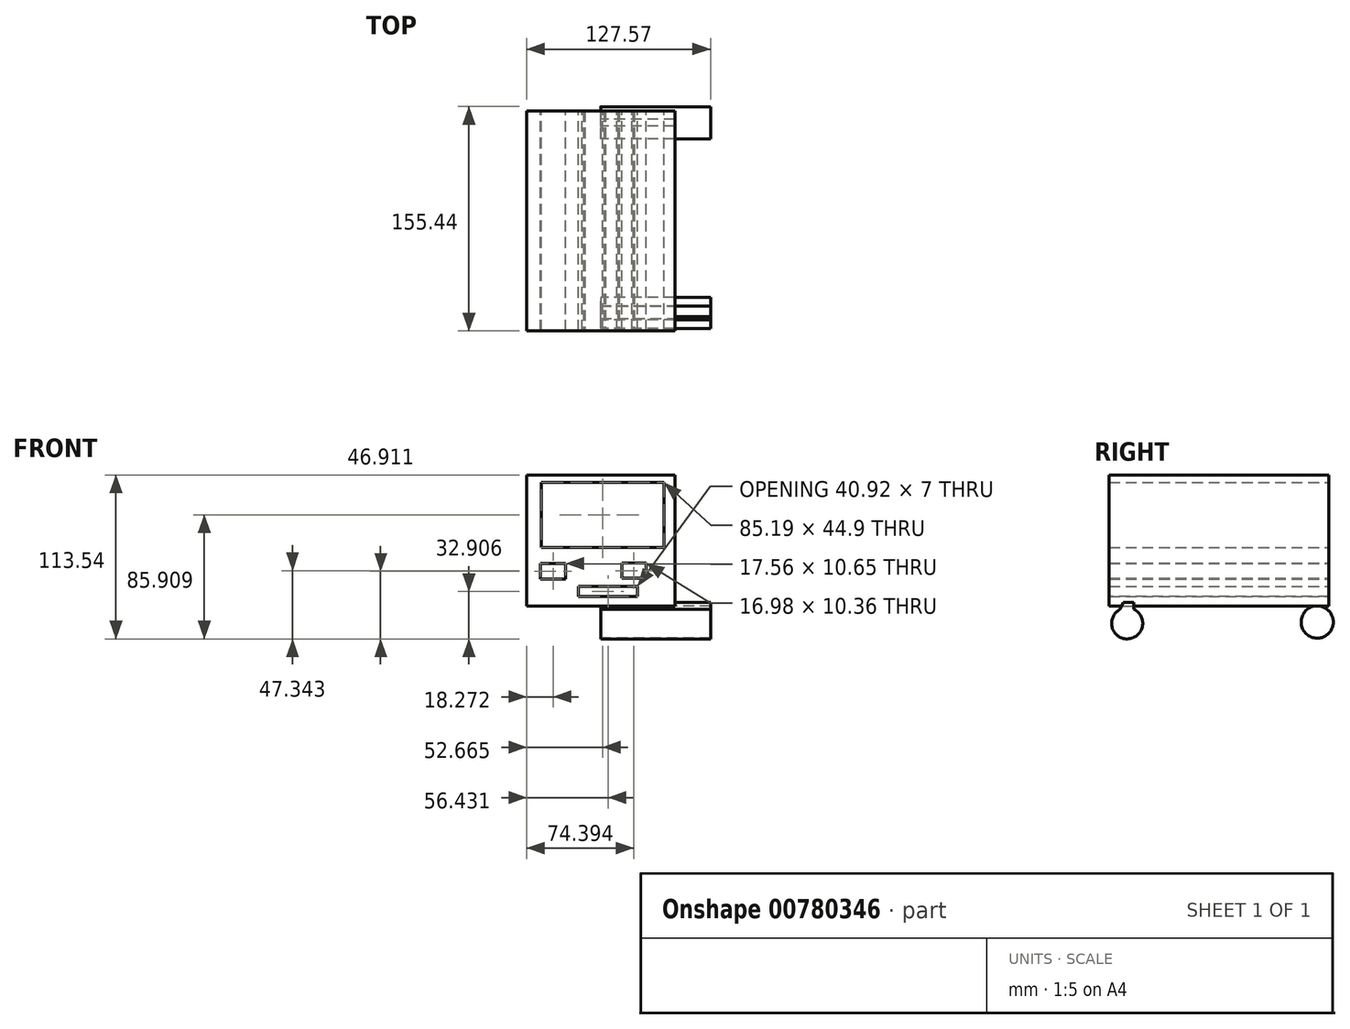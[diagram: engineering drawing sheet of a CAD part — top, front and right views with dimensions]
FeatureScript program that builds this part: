
annotation { "Feature Type Name" : "Feature", "Feature Type Description" : "" }
export const myFeature = defineFeature(function(context is Context, id is Id, definition is map)
    precondition{}
    {
        {
            var Q0;
            Q0=qCreatedBy(makeId("Front.planeOp"),FACE);
            var sketch = newSketch(context, id + "F0", { "sketchPlane" : qUnion([Q0])});
            skLineSegment(sketch, "E0.bottom", {"start": v(-51.37, 53.39) * mm, "end": v(51.37, 53.39) * mm});
            skLineSegment(sketch, "E0.top", {"start": v(-51.37, -37.56) * mm, "end": v(51.37, -37.56) * mm});
            skLineSegment(sketch, "E0.left", {"start": v(-51.37, 53.39) * mm, "end": v(-51.37, -37.56) * mm});
            skLineSegment(sketch, "E0.right", {"start": v(51.37, 53.39) * mm, "end": v(51.37, -37.56) * mm});
            skLineSegment(sketch, "E1.bottom", {"start": v(-41.88, -7.91) * mm, "end": v(-24.32, -7.91) * mm});
            skLineSegment(sketch, "E1.top", {"start": v(-41.88, -18.56) * mm, "end": v(-24.32, -18.56) * mm});
            skLineSegment(sketch, "E1.left", {"start": v(-41.88, -7.91) * mm, "end": v(-41.88, -18.56) * mm});
            skLineSegment(sketch, "E1.right", {"start": v(-24.32, -7.91) * mm, "end": v(-24.32, -18.56) * mm});
            skLineSegment(sketch, "E2.bottom", {"start": v(14.53, -7.63) * mm, "end": v(31.51, -7.63) * mm});
            skLineSegment(sketch, "E2.top", {"start": v(14.53, -17.99) * mm, "end": v(31.51, -17.99) * mm});
            skLineSegment(sketch, "E2.left", {"start": v(14.53, -7.63) * mm, "end": v(14.53, -17.99) * mm});
            skLineSegment(sketch, "E2.right", {"start": v(31.51, -7.63) * mm, "end": v(31.51, -17.99) * mm});
            skLineSegment(sketch, "E3.bottom", {"start": v(-15.4, -23.74) * mm, "end": v(25.52, -23.74) * mm});
            skLineSegment(sketch, "E3.top", {"start": v(-15.4, -30.65) * mm, "end": v(25.52, -30.65) * mm});
            skLineSegment(sketch, "E3.left", {"start": v(-15.4, -23.74) * mm, "end": v(-15.4, -30.65) * mm});
            skLineSegment(sketch, "E3.right", {"start": v(25.52, -23.74) * mm, "end": v(25.52, -30.65) * mm});
            skLineSegment(sketch, "E4.bottom", {"start": v(-41.88, -18.56) * mm, "end": v(-37.27, -18.56) * mm});
            skLineSegment(sketch, "E4.top", {"start": v(-41.88, -7.91) * mm, "end": v(-37.27, -7.91) * mm});
            skLineSegment(sketch, "E4.left", {"start": v(-41.88, -18.56) * mm, "end": v(-41.88, -7.91) * mm});
            skLineSegment(sketch, "E4.right", {"start": v(-37.27, -18.56) * mm, "end": v(-37.27, -7.91) * mm});
            skLineSegment(sketch, "E5.bottom", {"start": v(31.51, -17.99) * mm, "end": v(26.05, -17.99) * mm});
            skLineSegment(sketch, "E5.top", {"start": v(31.51, -7.63) * mm, "end": v(26.05, -7.63) * mm});
            skLineSegment(sketch, "E5.left", {"start": v(31.51, -17.99) * mm, "end": v(31.51, -7.63) * mm});
            skLineSegment(sketch, "E5.right", {"start": v(26.05, -17.99) * mm, "end": v(26.05, -7.63) * mm});
            skLineSegment(sketch, "E6", {"start": v(26.05, -12.8) * mm, "end": v(31.51, -12.8) * mm});
            skLineSegment(sketch, "E7", {"start": v(-41.88, -12.8) * mm, "end": v(-37.27, -12.8) * mm});
            skText(sketch, "E8", { "text": "UHG-675", "fontName": "Arimo-Bold.ttf"});
            skLineSegment(sketch, "E9.bottom", {"start": v(-41.3, 3.3) * mm, "end": v(43.9, 3.3) * mm});
            skLineSegment(sketch, "E9.top", {"start": v(-41.3, 48.2) * mm, "end": v(43.9, 48.2) * mm});
            skLineSegment(sketch, "E9.left", {"start": v(-41.3, 3.3) * mm, "end": v(-41.3, 48.2) * mm});
            skLineSegment(sketch, "E9.right", {"start": v(43.9, 3.3) * mm, "end": v(43.9, 48.2) * mm});
            const initialGuessF0  = {"E8": [-0.0154, -0.03065, 1, 0, 0.0069]};
            skSetInitialGuess(sketch, initialGuessF0);
            skSolve(sketch);
        }
        {
            var Q0;
            Q0 = qSketchRegion(id + "F0", true);
            extrude(context, id + "F1", {"entities" : qUnion([Q0]), "depth" : 152.4 * mm, "offsetDistance" : 25.4 * mm});
        }
        {
            var Q0;
            Q0=qCreatedBy(makeId("Right.planeOp"),FACE);
            var sketch = newSketch(context, id + "F2", { "sketchPlane" : qUnion([Q0])});
            skCircle(sketch, "E10", {"center": v(-8.14, -48.5) * mm, "radius": 11.18 * mm});
            skCircle(sketch, "E11", {"center": v(-139.96, -49.36) * mm, "radius": 10.79 * mm});
            skLineSegment(sketch, "E12", {"start": v(-144.9, -39.77) * mm, "end": v(-142.55, -34.97) * mm});
            skLineSegment(sketch, "E13", {"start": v(-135.24, -39.66) * mm, "end": v(-135.24, -34.97) * mm});
            skLineSegment(sketch, "E14", {"start": v(-135.24, -34.97) * mm, "end": v(-142.55, -34.97) * mm});
            skSolve(sketch);
        }
        {
            var Q0;
            Q0 = qSketchRegion(id + "F2", true);
            extrude(context, id + "F3", {"entities" : qUnion([Q0]), "operationType" : NewBodyOperationType.ADD, "depth" : 76.2 * mm, "offsetDistance" : 25.4 * mm});
        }
    });
